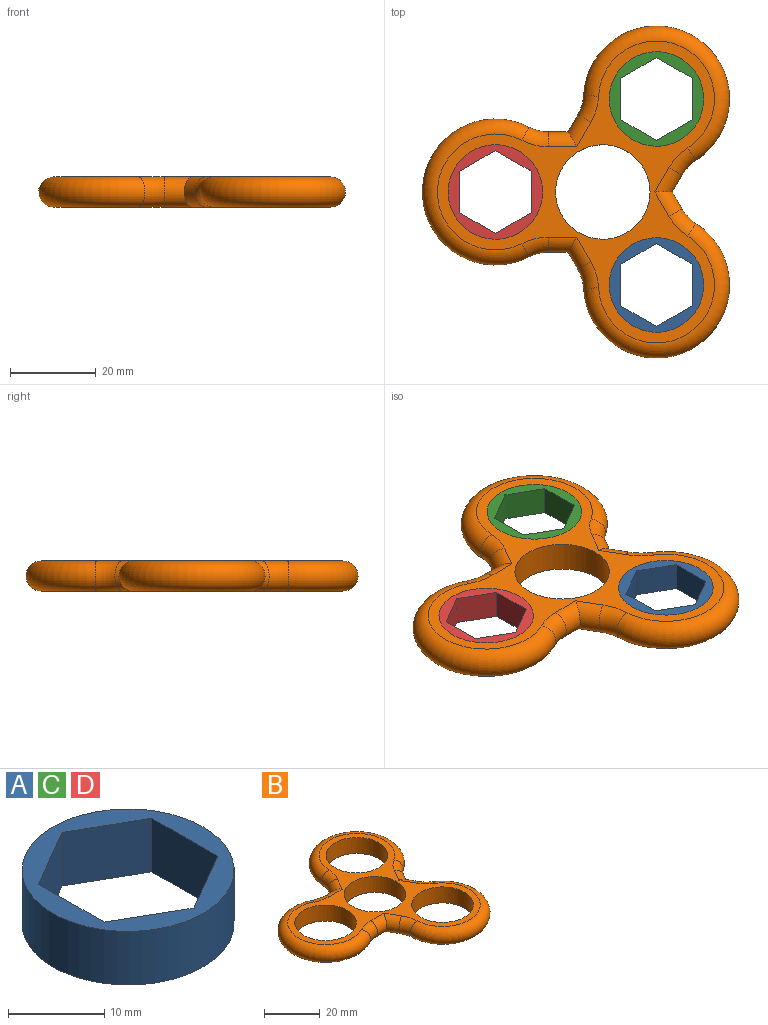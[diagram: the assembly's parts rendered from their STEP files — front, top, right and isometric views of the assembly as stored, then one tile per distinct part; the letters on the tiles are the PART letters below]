
ASSEMBLY  parts=4 mates=3
PART A: 9 faces, bbox 22x22x6.8 mm
  f0: plane 9.64x6.8mm, normal (1,0,0), area 65.6mm2, adj f1,f5,f7,f8
  f1: plane 8.33x6.8mm, normal (0.5,-0.86,0), area 65.6mm2, adj f0,f2,f7,f8
  f2: plane 8.37x6.8mm, normal (-0.5,-0.87,0), area 65.6mm2, adj f1,f3,f7,f8
  f3: plane 9.64x6.8mm, normal (-1,0,0), area 65.6mm2, adj f2,f4,f7,f8
  f4: plane 8.33x6.8mm, normal (-0.5,0.86,0), area 65.6mm2, adj f3,f5,f7,f8
  f5: plane 8.37x6.8mm, normal (0.5,0.87,0), area 65.6mm2, adj f0,f4,f7,f8
  f6: cylinder r=11mm len=22mm, axis (0,0,-1), area 470mm2, adj f7,f8
  f7: plane 22x22mm, normal (0,0,1), area 138.6mm2, adj f0,f1,f2,f3,f4,f5,f6
  f8: plane 22x22mm, normal (0,0,-1), area 138.6mm2, adj f0,f1,f2,f3,f4,f5,f6
PART B: 21 faces, bbox 74.3x80.1x7 mm
  f0: cylinder r=11mm len=22mm, axis (0,0,-1), area 483.8mm2, adj f2,f3
  f1: cylinder r=11mm len=22mm, axis (0,0,-1), area 483.8mm2, adj f2,f3
  f2: plane 70.3x64.5mm, normal (0,0,1), area 833.7mm2, adj f0,f1,f4,f5,f6,f7,f8,f9
  f3: plane 70.3x64.5mm, normal (0,0,-1), area 833.7mm2, adj f0,f1,f4,f5,f6,f7,f8,f9
  f4: cylinder r=11mm len=22mm, axis (0,0,-1), area 483.8mm2, adj f2,f3
  f5: cylinder r=11mm len=22mm, axis (0,0,-1), area 483.8mm2, adj f2,f3
  f6: cylinder r=3.5mm len=7.44mm, axis (0.5,0.87,0), area 58.1mm2, adj f2,f3,f7,f8
  f7: torus R=13.5mm, axis (0,0,1), area 59mm2, adj f2,f3,f6,f9
  f8: cylinder r=3.5mm len=7mm, axis (1,0,0), area 58.1mm2, adj f2,f3,f6,f10
  f9: torus R=13.5mm, axis (0,0,1), area 707.9mm2, adj f2,f3,f7,f11
  f10: torus R=13.5mm, axis (0,0,1), area 59mm2, adj f2,f3,f8,f12
  f11: torus R=13.5mm, axis (0,0,1), area 59mm2, adj f2,f3,f9,f13
  f12: torus R=13.5mm, axis (0,0,1), area 707.9mm2, adj f2,f3,f10,f14
  f13: cylinder r=3.5mm len=7.44mm, axis (-0.5,-0.87,0), area 58.1mm2, adj f2,f3,f11,f15
  f14: torus R=13.5mm, axis (0,0,1), area 59mm2, adj f2,f3,f12,f16
  f15: cylinder r=3.5mm len=7.44mm, axis (0.5,-0.87,0), area 58.1mm2, adj f2,f3,f13,f17
  f16: cylinder r=3.5mm len=7mm, axis (-1,0,0), area 58.1mm2, adj f2,f3,f14,f18
  f17: torus R=13.5mm, axis (0,0,1), area 59mm2, adj f2,f3,f15,f19
  f18: cylinder r=3.5mm len=7.44mm, axis (-0.5,0.87,0), area 58.1mm2, adj f2,f3,f16,f20
  f19: torus R=13.5mm, axis (0,0,1), area 707.9mm2, adj f2,f3,f17,f20
  f20: torus R=13.5mm, axis (0,0,1), area 59mm2, adj f2,f3,f18,f19
PART C: same geometry as A
PART D: same geometry as A
PLACE A t=(-15.94,-41.05,3.71)mm
PLACE B t=(-28.44,-19.4,3.51)mm
PLACE C t=(-15.94,2.25,3.71)mm
PLACE D t=(-53.44,-19.4,3.71)mm
MATE revolute C.f6 <-> B.f4  axis (0,0,1) through (-15.94,2.25,10.51)mm
MATE fastened D.f6 <-> B.f0  axis (0,0,1) through (-53.44,-19.4,10.51)mm
MATE revolute A.f6 <-> B.f5  axis (0,0,1) through (-15.94,-41.05,10.51)mm
